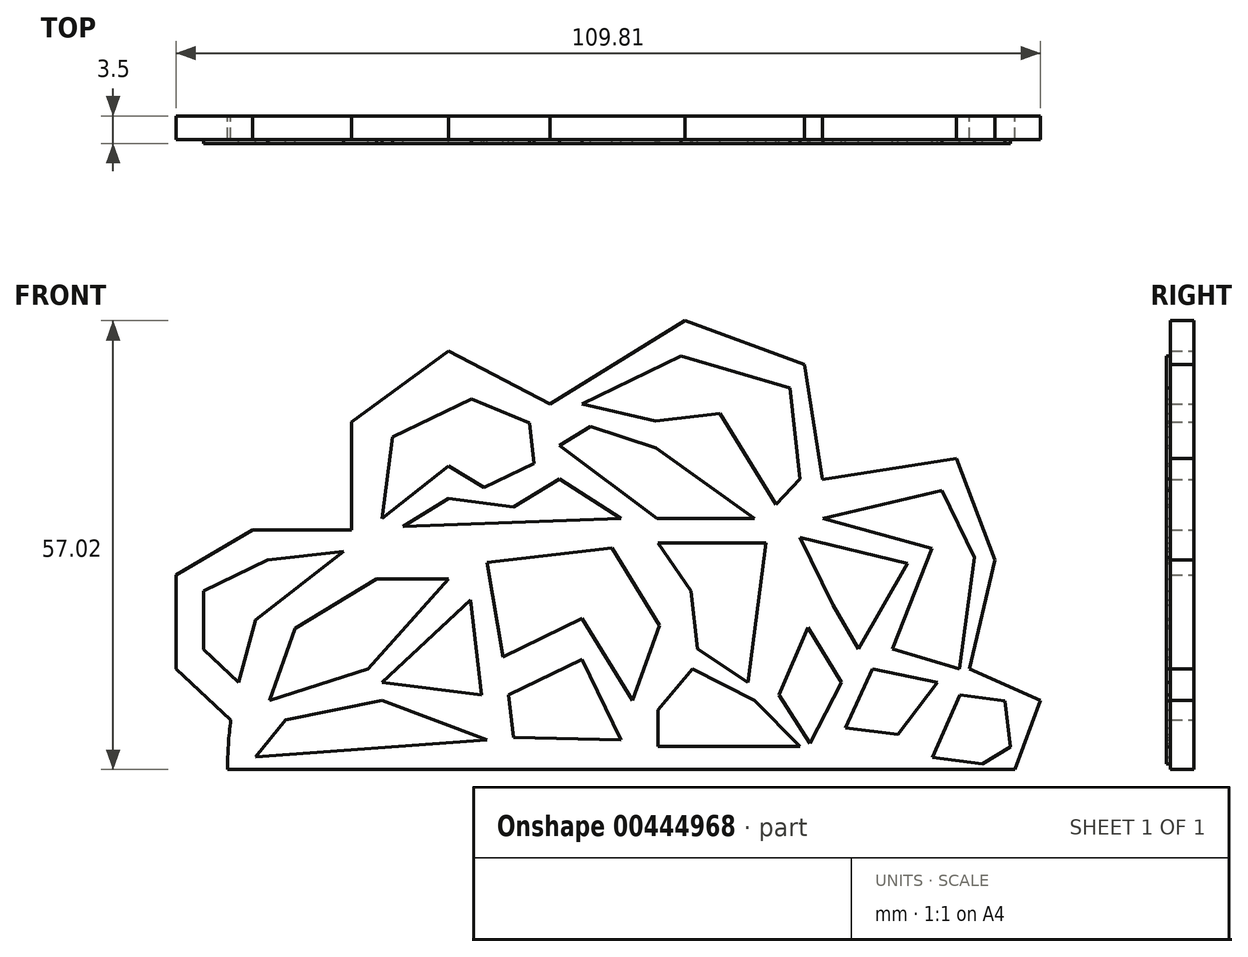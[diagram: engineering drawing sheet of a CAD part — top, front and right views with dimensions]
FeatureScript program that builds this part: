
annotation { "Feature Type Name" : "Feature", "Feature Type Description" : "" }
export const myFeature = defineFeature(function(context is Context, id is Id, definition is map)
    precondition{}
    {
        {
            var Q0;
            Q0=qCreatedBy(makeId("Front.planeOp"),FACE);
            var sketch = newSketch(context, id + "F0", { "sketchPlane" : qUnion([Q0])});
            skLineSegment(sketch, "E0", {"start": v(-50, 0) * mm, "end": v(50, 0) * mm});
            skLineSegment(sketch, "E1", {"start": v(-49.6, 6.3) * mm, "end": v(-56.54, 12.79) * mm});
            skLineSegment(sketch, "E2", {"start": v(-56.54, 12.79) * mm, "end": v(-56.54, 24.71) * mm});
            skLineSegment(sketch, "E3", {"start": v(-56.54, 24.71) * mm, "end": v(-46.85, 30.42) * mm});
            skLineSegment(sketch, "E4", {"start": v(-46.85, 30.42) * mm, "end": v(-34.23, 30.42) * mm});
            skLineSegment(sketch, "E5", {"start": v(-34.23, 30.42) * mm, "end": v(-34.23, 44.13) * mm});
            skLineSegment(sketch, "E6", {"start": v(-34.23, 44.13) * mm, "end": v(-21.92, 53.17) * mm});
            skLineSegment(sketch, "E7", {"start": v(-21.92, 53.17) * mm, "end": v(-9.04, 46.44) * mm});
            skLineSegment(sketch, "E8", {"start": v(-9.04, 46.44) * mm, "end": v(8.08, 57.02) * mm});
            skLineSegment(sketch, "E9", {"start": v(8.08, 57.02) * mm, "end": v(23.27, 51.44) * mm});
            skLineSegment(sketch, "E10", {"start": v(23.27, 51.44) * mm, "end": v(25.58, 36.83) * mm});
            skLineSegment(sketch, "E11", {"start": v(25.58, 36.83) * mm, "end": v(42.6, 39.52) * mm});
            skLineSegment(sketch, "E12", {"start": v(42.6, 39.52) * mm, "end": v(47.5, 26.63) * mm});
            skLineSegment(sketch, "E13", {"start": v(47.5, 26.63) * mm, "end": v(44.23, 12.79) * mm});
            skLineSegment(sketch, "E14", {"start": v(44.23, 12.79) * mm, "end": v(53.27, 8.75) * mm});
            skLineSegment(sketch, "E15", {"start": v(53.27, 8.75) * mm, "end": v(50, 0) * mm});
            skArc(sketch, "E16.trimOffspring", {"start": v(-49.6, 6.3) * mm, "mid": v(-49.9, 3.16) * mm, "end": v(-50, 0) * mm});
            skSolve(sketch);
        }
        {
            var Q0;
            Q0 = qSketchRegion(id + "F0", true);
            extrude(context, id + "F1", {"entities" : qUnion([Q0]), "depth" : 3 * mm});
        }
        {
            var Q0;
            Q0=makeQuery(id+"F1.opExtrude","CAP_FACE",FACE,{"disambiguationData":[OSD([sQuery(id+"F0.wireOp",EDGE,"E0"),sQuery(id+"F0.wireOp",EDGE,"E1"),sQuery(id+"F0.wireOp",EDGE,"E2"),sQuery(id+"F0.wireOp",EDGE,"E3"),sQuery(id+"F0.wireOp",EDGE,"E4"),sQuery(id+"F0.wireOp",EDGE,"E5"),sQuery(id+"F0.wireOp",EDGE,"E6"),sQuery(id+"F0.wireOp",EDGE,"E7"),sQuery(id+"F0.wireOp",EDGE,"E8"),sQuery(id+"F0.wireOp",EDGE,"E9"),sQuery(id+"F0.wireOp",EDGE,"E10"),sQuery(id+"F0.wireOp",EDGE,"E11"),sQuery(id+"F0.wireOp",EDGE,"E12"),sQuery(id+"F0.wireOp",EDGE,"E13"),sQuery(id+"F0.wireOp",EDGE,"E14"),sQuery(id+"F0.wireOp",EDGE,"E15"),sQuery(id+"F0.wireOp",EDGE,"E16.trimOffspring")])],"isStart":false});
            var sketch = newSketch(context, id + "F2", { "sketchPlane" : qUnion([Q0])});
            skLineSegment(sketch, "E17", {"start": v(-48.62, 11.1) * mm, "end": v(-53.07, 15.26) * mm});
            skPoint(sketch, "E17.endSnap0", {"position": v(-53.07, 9.54) * mm});
            skLineSegment(sketch, "E18", {"start": v(-53.07, 15.26) * mm, "end": v(-53.07, 22.65) * mm});
            skLineSegment(sketch, "E19", {"start": v(-53.07, 22.65) * mm, "end": v(-44.95, 26.6) * mm});
            skLineSegment(sketch, "E20", {"start": v(-44.95, 26.6) * mm, "end": v(-35.3, 27.69) * mm});
            skLineSegment(sketch, "E21", {"start": v(-35.3, 27.69) * mm, "end": v(-46.45, 18.98) * mm});
            skLineSegment(sketch, "E22", {"start": v(-46.45, 18.98) * mm, "end": v(-48.62, 11.1) * mm});
            skLineSegment(sketch, "E23", {"start": v(-30.4, 31.9) * mm, "end": v(-29.04, 42.24) * mm});
            skLineSegment(sketch, "E24", {"start": v(-29.04, 42.24) * mm, "end": v(-19.03, 47.1) * mm});
            skLineSegment(sketch, "E25", {"start": v(-19.03, 47.1) * mm, "end": v(-11.63, 44) * mm});
            skLineSegment(sketch, "E26", {"start": v(-11.63, 44) * mm, "end": v(-11.06, 38.9) * mm});
            skLineSegment(sketch, "E27", {"start": v(-11.06, 38.9) * mm, "end": v(-17.4, 35.82) * mm});
            skLineSegment(sketch, "E28", {"start": v(-17.4, 35.82) * mm, "end": v(-21.92, 38.56) * mm});
            skLineSegment(sketch, "E29", {"start": v(-21.92, 38.56) * mm, "end": v(-30.4, 31.9) * mm});
            skLineSegment(sketch, "E30", {"start": v(-4.97, 46.44) * mm, "end": v(7.62, 52.56) * mm});
            skLineSegment(sketch, "E31", {"start": v(7.62, 52.56) * mm, "end": v(21.4, 48.5) * mm});
            skLineSegment(sketch, "E32", {"start": v(21.4, 48.5) * mm, "end": v(22.72, 36.9) * mm});
            skLineSegment(sketch, "E33", {"start": v(22.72, 36.9) * mm, "end": v(19.64, 33.67) * mm});
            skLineSegment(sketch, "E34", {"start": v(19.64, 33.67) * mm, "end": v(12.57, 45.23) * mm});
            skLineSegment(sketch, "E35", {"start": v(12.57, 45.23) * mm, "end": v(4.38, 44.3) * mm});
            skLineSegment(sketch, "E36", {"start": v(4.38, 44.3) * mm, "end": v(-4.97, 46.44) * mm});
            skLineSegment(sketch, "E37", {"start": v(25.62, 31.9) * mm, "end": v(40.72, 35.44) * mm});
            skLineSegment(sketch, "E38", {"start": v(40.72, 35.44) * mm, "end": v(44.84, 26.95) * mm});
            skLineSegment(sketch, "E39", {"start": v(44.84, 26.95) * mm, "end": v(42.97, 12.79) * mm});
            skLineSegment(sketch, "E40", {"start": v(42.97, 12.79) * mm, "end": v(34.46, 15.31) * mm});
            skLineSegment(sketch, "E41", {"start": v(34.46, 15.31) * mm, "end": v(39.5, 28.1) * mm});
            skLineSegment(sketch, "E42", {"start": v(39.5, 28.1) * mm, "end": v(25.62, 31.9) * mm});
            skLineSegment(sketch, "E43", {"start": v(43.03, 9.46) * mm, "end": v(48.75, 8.71) * mm});
            skPoint(sketch, "E43.endSnap0", {"position": v(48.75, 10.77) * mm});
            skLineSegment(sketch, "E44", {"start": v(48.75, 8.71) * mm, "end": v(49.41, 2.85) * mm});
            skLineSegment(sketch, "E45", {"start": v(49.41, 2.85) * mm, "end": v(45.9, 0.7) * mm});
            skLineSegment(sketch, "E46", {"start": v(45.9, 0.7) * mm, "end": v(39.5, 1.54) * mm});
            skLineSegment(sketch, "E47", {"start": v(39.5, 1.54) * mm, "end": v(43.03, 9.46) * mm});
            skLineSegment(sketch, "E48", {"start": v(40.17, 11.1) * mm, "end": v(35.14, 4.43) * mm});
            skLineSegment(sketch, "E49", {"start": v(35.14, 4.43) * mm, "end": v(28.48, 5.3) * mm});
            skLineSegment(sketch, "E50", {"start": v(28.48, 5.3) * mm, "end": v(31.88, 12.79) * mm});
            skLineSegment(sketch, "E51", {"start": v(31.88, 12.79) * mm, "end": v(40.17, 11.1) * mm});
            skLineSegment(sketch, "E52", {"start": v(30.11, 15.31) * mm, "end": v(36.37, 26.19) * mm});
            skLineSegment(sketch, "E53", {"start": v(36.37, 26.19) * mm, "end": v(22.72, 29.45) * mm});
            skLineSegment(sketch, "E54", {"start": v(22.72, 29.45) * mm, "end": v(26.87, 20.9) * mm});
            skLineSegment(sketch, "E55", {"start": v(26.87, 20.9) * mm, "end": v(30.11, 15.31) * mm});
            skLineSegment(sketch, "E56", {"start": v(16.92, 31.9) * mm, "end": v(4.41, 40.88) * mm});
            skLineSegment(sketch, "E57", {"start": v(4.41, 40.88) * mm, "end": v(-3.88, 43.6) * mm});
            skLineSegment(sketch, "E58", {"start": v(-3.88, 43.6) * mm, "end": v(-7.85, 41.17) * mm});
            skLineSegment(sketch, "E59", {"start": v(-7.85, 41.17) * mm, "end": v(4.55, 31.9) * mm});
            skLineSegment(sketch, "E60", {"start": v(4.55, 31.9) * mm, "end": v(16.92, 31.9) * mm});
            skLineSegment(sketch, "E61", {"start": v(0, 31.9) * mm, "end": v(-7.83, 36.9) * mm});
            skLineSegment(sketch, "E62", {"start": v(-7.83, 36.9) * mm, "end": v(-13.66, 33.33) * mm});
            skLineSegment(sketch, "E63", {"start": v(-13.66, 33.33) * mm, "end": v(-21.92, 34.42) * mm});
            skLineSegment(sketch, "E64", {"start": v(-21.92, 34.42) * mm, "end": v(-27.74, 30.86) * mm});
            skLineSegment(sketch, "E65", {"start": v(-27.74, 30.86) * mm, "end": v(0, 31.9) * mm});
            skLineSegment(sketch, "E66", {"start": v(-44.68, 8.75) * mm, "end": v(-41.41, 17.9) * mm});
            skLineSegment(sketch, "E67", {"start": v(-41.41, 17.9) * mm, "end": v(-31.08, 24.22) * mm});
            skLineSegment(sketch, "E68", {"start": v(-31.08, 24.22) * mm, "end": v(-21.92, 24.22) * mm});
            skLineSegment(sketch, "E69", {"start": v(-21.92, 24.22) * mm, "end": v(-32.17, 12.79) * mm});
            skLineSegment(sketch, "E70", {"start": v(-32.17, 12.79) * mm, "end": v(-44.68, 8.75) * mm});
            skLineSegment(sketch, "E71", {"start": v(-17.07, 26.33) * mm, "end": v(-1.15, 28.12) * mm});
            skLineSegment(sketch, "E72", {"start": v(-1.15, 28.12) * mm, "end": v(4.86, 18.3) * mm});
            skLineSegment(sketch, "E73", {"start": v(4.86, 18.3) * mm, "end": v(1.42, 8.75) * mm});
            skLineSegment(sketch, "E74", {"start": v(1.42, 8.75) * mm, "end": v(-4.97, 19.2) * mm});
            skLineSegment(sketch, "E75", {"start": v(-4.97, 19.2) * mm, "end": v(-15.01, 14.32) * mm});
            skLineSegment(sketch, "E76", {"start": v(-15.01, 14.32) * mm, "end": v(-17.07, 26.33) * mm});
            skLineSegment(sketch, "E77", {"start": v(-30.4, 11.1) * mm, "end": v(-19.11, 21.57) * mm});
            skLineSegment(sketch, "E78", {"start": v(-19.11, 21.57) * mm, "end": v(-17.75, 9.46) * mm});
            skLineSegment(sketch, "E79", {"start": v(-17.75, 9.46) * mm, "end": v(-30.4, 11.1) * mm});
            skLineSegment(sketch, "E80", {"start": v(4.68, 28.77) * mm, "end": v(18.42, 28.77) * mm});
            skLineSegment(sketch, "E81", {"start": v(18.42, 28.77) * mm, "end": v(16.1, 11.1) * mm});
            skLineSegment(sketch, "E82", {"start": v(16.1, 11.1) * mm, "end": v(9.71, 15.31) * mm});
            skLineSegment(sketch, "E83", {"start": v(9.71, 15.31) * mm, "end": v(8.89, 22.65) * mm});
            skLineSegment(sketch, "E84", {"start": v(8.89, 22.65) * mm, "end": v(4.68, 28.77) * mm});
            skLineSegment(sketch, "E85", {"start": v(20.05, 9.46) * mm, "end": v(23.72, 18.03) * mm});
            skLineSegment(sketch, "E86", {"start": v(23.72, 18.03) * mm, "end": v(27.96, 11.1) * mm});
            skLineSegment(sketch, "E87", {"start": v(27.96, 11.1) * mm, "end": v(24, 3.34) * mm});
            skLineSegment(sketch, "E88", {"start": v(24, 3.34) * mm, "end": v(20.05, 9.46) * mm});
            skLineSegment(sketch, "E89", {"start": v(4.68, 7.56) * mm, "end": v(9.03, 12.79) * mm});
            skLineSegment(sketch, "E90", {"start": v(9.03, 12.79) * mm, "end": v(16.92, 8.75) * mm});
            skLineSegment(sketch, "E91", {"start": v(16.92, 8.75) * mm, "end": v(22.72, 2.94) * mm});
            skLineSegment(sketch, "E92", {"start": v(22.72, 2.94) * mm, "end": v(4.68, 2.94) * mm});
            skLineSegment(sketch, "E93", {"start": v(4.68, 2.94) * mm, "end": v(4.68, 7.56) * mm});
            skLineSegment(sketch, "E94", {"start": v(0, 3.75) * mm, "end": v(-4.97, 13.99) * mm});
            skLineSegment(sketch, "E95", {"start": v(-4.97, 13.99) * mm, "end": v(-14.29, 9.46) * mm});
            skLineSegment(sketch, "E96", {"start": v(-14.29, 9.46) * mm, "end": v(-13.68, 4.1) * mm});
            skLineSegment(sketch, "E97", {"start": v(-13.68, 4.1) * mm, "end": v(0, 3.75) * mm});
            skLineSegment(sketch, "E98", {"start": v(-17.07, 3.75) * mm, "end": v(-30.4, 8.75) * mm});
            skLineSegment(sketch, "E99", {"start": v(-30.4, 8.75) * mm, "end": v(-42.64, 6.3) * mm});
            skLineSegment(sketch, "E100", {"start": v(-42.64, 6.3) * mm, "end": v(-46.45, 1.58) * mm});
            skLineSegment(sketch, "E101", {"start": v(-46.45, 1.58) * mm, "end": v(-17.07, 3.75) * mm});
            skSolve(sketch);
        }
        {
            var Q0;
            Q0 = qSketchRegion(id + "F2", true);
            extrude(context, id + "F3", {"entities" : qUnion([Q0]), "operationType" : NewBodyOperationType.ADD, "depth" : 0.5 * mm});
        }
    });
